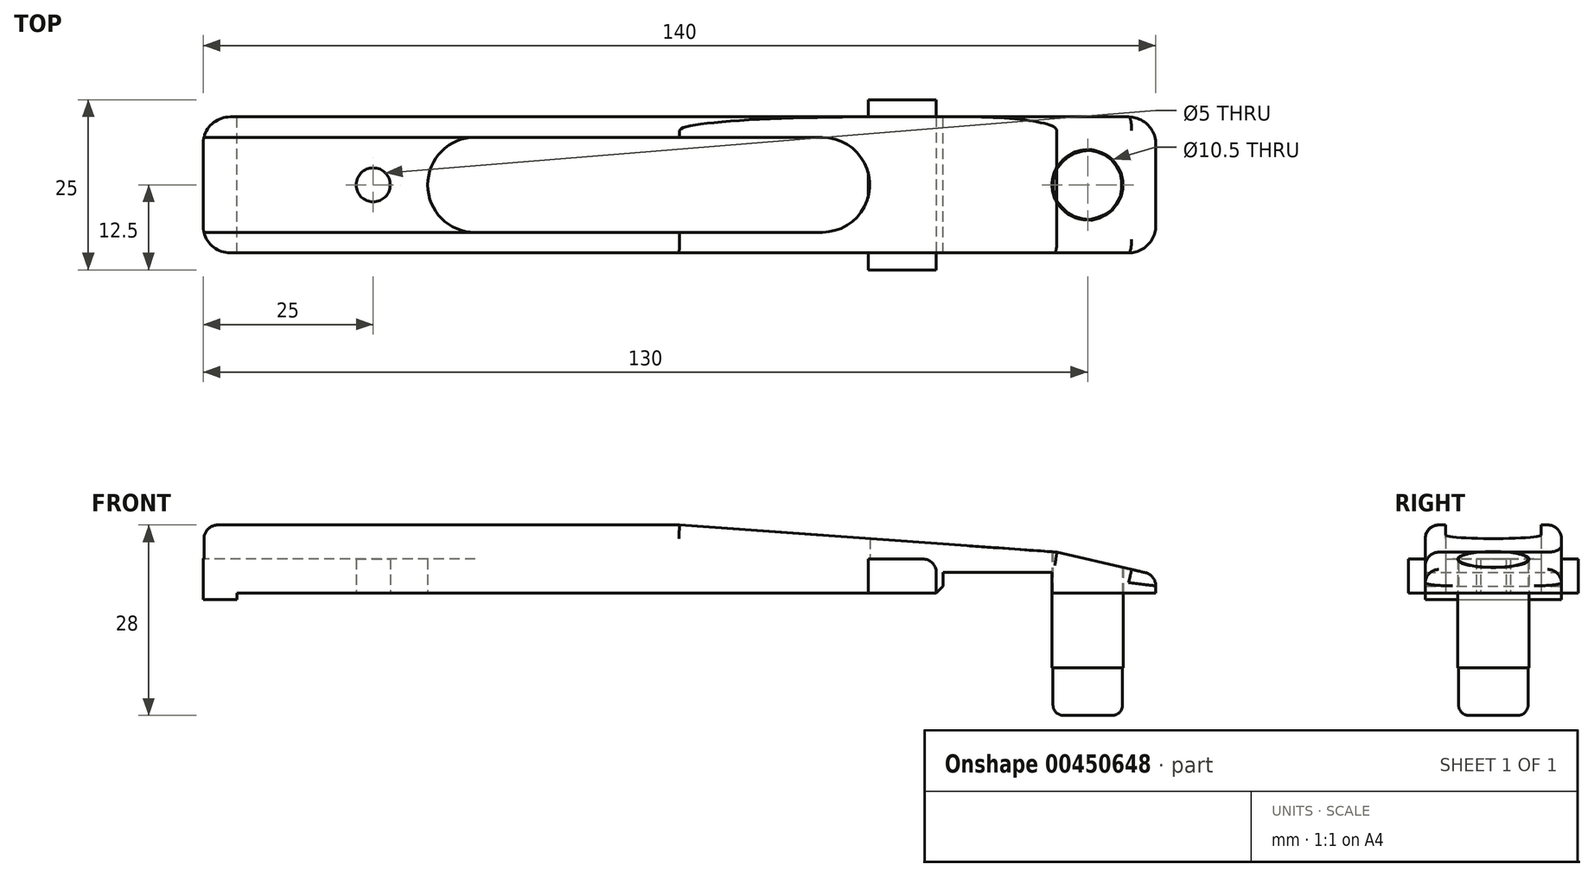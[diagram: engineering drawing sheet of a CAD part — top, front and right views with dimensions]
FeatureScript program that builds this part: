
annotation { "Feature Type Name" : "Feature", "Feature Type Description" : "" }
export const myFeature = defineFeature(function(context is Context, id is Id, definition is map)
    precondition{}
    {
        {
            var Q0;
            Q0=qCreatedBy(makeId("Top.planeOp"),FACE);
            var sketch = newSketch(context, id + "F0", { "sketchPlane" : qUnion([Q0])});
            skLineSegment(sketch, "E0.bottom", {"start": v(66, -10) * mm, "end": v(-66, -10) * mm});
            skLineSegment(sketch, "E0.top", {"start": v(66, 10) * mm, "end": v(-66, 10) * mm});
            skLineSegment(sketch, "E0.left", {"start": v(70, -6) * mm, "end": v(70, 6) * mm});
            skLineSegment(sketch, "E0.right", {"start": v(-70, -6) * mm, "end": v(-70, 6) * mm});
            skPoint(sketch, "E0.middle", {"position": v(0, 0) * mm});
            skCircle(sketch, "E1", {"center": v(-45, 0) * mm, "radius": 2.5 * mm});
            skArc(sketch, "E2", {"start": v(-30, 7) * mm, "mid": v(-37, 0) * mm, "end": v(-30, -7) * mm});
            skArc(sketch, "E3", {"start": v(21, -7) * mm, "mid": v(28, 0) * mm, "end": v(21, 7) * mm});
            skLineSegment(sketch, "E4", {"start": v(-30, 7) * mm, "end": v(21, 7) * mm});
            skLineSegment(sketch, "E5", {"start": v(21, -7) * mm, "end": v(-30, -7) * mm});
            skCircle(sketch, "E6", {"center": v(60, 0) * mm, "radius": 5.1 * mm});
            skPoint(sketch, "E7.visualSharp", {"position": v(-70, 10) * mm});
            skArc(sketch, "E7.filletArc", {"start": v(-66, 10) * mm, "mid": v(-68.83, 8.83) * mm, "end": v(-70, 6) * mm});
            skPoint(sketch, "E8.visualSharp", {"position": v(-70, -10) * mm});
            skArc(sketch, "E8.filletArc", {"start": v(-70, -6) * mm, "mid": v(-68.83, -8.83) * mm, "end": v(-66, -10) * mm});
            skPoint(sketch, "E9.visualSharp", {"position": v(70, 10) * mm});
            skArc(sketch, "E9.filletArc", {"start": v(70, 6) * mm, "mid": v(68.83, 8.83) * mm, "end": v(66, 10) * mm});
            skPoint(sketch, "E10.visualSharp", {"position": v(70, -10) * mm});
            skArc(sketch, "E10.filletArc", {"start": v(66, -10) * mm, "mid": v(68.83, -8.83) * mm, "end": v(70, -6) * mm});
            skCircle(sketch, "E11", {"center": v(60, 0) * mm, "radius": 5.25 * mm});
            skSolve(sketch);
        }
        {
            var Q0;
            Q0=makeQuery(id+"F0.imprint","IMPRINT",FACE,{"disambiguationData":[TD([[makeQuery(id+"F0.imprint","IMPRINT",EDGE,{"derivedFrom":sQuery(id+"F0.wireOp",EDGE,"E0.bottom")}),-1.0]])]});
            extrude(context, id + "F1", {"entities" : qUnion([Q0]), "depth" : 10 * mm, "offsetDistance" : 25 * mm});
        }
        {
            var Q0;
            Q0=makeQuery(id+"F0.imprint","IMPRINT",FACE,{"disambiguationData":[TD([[makeQuery(id+"F0.imprint","IMPRINT",EDGE,{"derivedFrom":sQuery(id+"F0.wireOp",EDGE,"E6")}),1.0]])]});
            extrude(context, id + "F2", {"entities" : qUnion([Q0]), "operationType" : NewBodyOperationType.ADD, "depth" : 10 * mm, "hasSecondDirection" : true, "secondDirectionOppositeDirection" : true, "secondDirectionDepth" : 18 * mm, "offsetDistance" : 25 * mm});
        }
        {
            var Q0;
            Q0=makeQuery(id+"F1.opExtrude","SWEPT_FACE",FACE,{"disambiguationData":[OSD([sQuery(id+"F0.wireOp",EDGE,"E0.right")])]});
            var sketch = newSketch(context, id + "F3", { "sketchPlane" : qUnion([Q0])});
            skLineSegment(sketch, "E12.bottom", {"start": v(-6, 10) * mm, "end": v(7, 10) * mm});
            skLineSegment(sketch, "E12.top", {"start": v(-7, 5) * mm, "end": v(6, 5) * mm});
            skLineSegment(sketch, "E12.left", {"start": v(-7, 10) * mm, "end": v(-7, 5) * mm});
            skLineSegment(sketch, "E12.right", {"start": v(7, 10) * mm, "end": v(7, 5) * mm});
            skLineSegment(sketch, "E13", {"start": v(-7, 10) * mm, "end": v(-6, 10) * mm});
            skLineSegment(sketch, "E14", {"start": v(7, 10) * mm, "end": v(6, 10) * mm});
            skLineSegment(sketch, "E15", {"start": v(7, 5) * mm, "end": v(6, 5) * mm});
            skSolve(sketch);
        }
        {
            var Q0;
            Q0=makeQuery(id+"F3.imprint","IMPRINT",FACE,{"disambiguationData":[TD([[makeQuery(id+"F3.imprint","IMPRINT",EDGE,{"derivedFrom":sQuery(id+"F3.wireOp",EDGE,"E12.bottom")}),1.0]])]});
            var Q1;
            Q1=makeQuery(id+"F3.imprint","IMPRINT",FACE,{"disambiguationData":[TD([[makeQuery(id+"F3.imprint","IMPRINT",EDGE,{"derivedFrom":sQuery(id+"F3.wireOp",EDGE,"E12.right")}),-1.0]])]});
            var Q2;
            {var subQ0=sQuery(id+"F3.wireOp",EDGE,"E12.left");Q2=makeQuery(id+"F3.imprint","IMPRINT",FACE,{"disambiguationData":[TD([[makeQuery(id+"F3.imprint","IMPRINT",EDGE,{"derivedFrom":subQ0}),1.0]])]});}
            extrude(context, id + "F4", {"entities" : qUnion([Q0, Q1, Q2]), "operationType" : NewBodyOperationType.REMOVE, "oppositeDirection" : true, "depth" : 90 * mm});
        }
        {
            var Q0;
            Q0=makeQuery(id+"F1.opExtrude","SWEPT_FACE",FACE,{"disambiguationData":[OSD([sQuery(id+"F0.wireOp",EDGE,"E0.top")])]});
            var sketch = newSketch(context, id + "F5", { "sketchPlane" : qUnion([Q0])});
            skLineSegment(sketch, "E16", {"start": v(-54.74, 0) * mm, "end": v(-54.74, 3) * mm});
            skLineSegment(sketch, "E17", {"start": v(-54.74, 3) * mm, "end": v(-38.74, 3) * mm});
            skLineSegment(sketch, "E18", {"start": v(-38.74, 3) * mm, "end": v(-38.74, 0) * mm});
            skLineSegment(sketch, "E19", {"start": v(-38.74, 0) * mm, "end": v(-54.74, 0) * mm});
            skSolve(sketch);
        }
        {
            var Q0;
            Q0=makeQuery(id+"F5.imprint","IMPRINT",FACE,{"disambiguationData":[TD([[makeQuery(id+"F5.imprint","IMPRINT",EDGE,{"derivedFrom":sQuery(id+"F5.wireOp",EDGE,"E16")}),-1.0]])]});
            extrude(context, id + "F6", {"entities" : qUnion([Q0]), "operationType" : NewBodyOperationType.REMOVE, "oppositeDirection" : true, "depth" : 25 * mm, "offsetDistance" : 25 * mm});
        }
        {
            var Q0;
            Q0=makeQuery(id+"F1.opExtrude","SWEPT_FACE",FACE,{"disambiguationData":[OSD([sQuery(id+"F0.wireOp",EDGE,"E0.top")])]});
            var sketch = newSketch(context, id + "F7", { "sketchPlane" : qUnion([Q0])});
            skLineSegment(sketch, "E20", {"start": v(-81.34, 0) * mm, "end": v(-55.47, 6) * mm});
            skPoint(sketch, "E20.startSnap0", {"position": v(-66, 6) * mm});
            skLineSegment(sketch, "E21", {"start": v(-55.47, 6) * mm, "end": v(0, 10) * mm});
            skLineSegment(sketch, "E22", {"start": v(0, 10) * mm, "end": v(-0.81, 21.29) * mm});
            skLineSegment(sketch, "E23", {"start": v(-0.81, 21.29) * mm, "end": v(-86.16, 20.04) * mm});
            skLineSegment(sketch, "E24", {"start": v(-86.16, 20.04) * mm, "end": v(-81.34, 0) * mm});
            skSolve(sketch);
        }
        {
            var Q0;
            {var subQ4=sQuery(id+"F7.wireOp",EDGE,"E22");Q0=makeQuery(id+"F7.imprint","IMPRINT",FACE,{"disambiguationData":[TD([[makeQuery(id+"F7.imprint","IMPRINT",EDGE,{"derivedFrom":subQ4}),1.0]])]});}
            var Q1;
            {var subQ0=sQuery(id+"F7.wireOp",EDGE,"E21");Q1=makeQuery(id+"F7.imprint","IMPRINT",FACE,{"disambiguationData":[TD([[makeQuery(id+"F7.imprint","IMPRINT",EDGE,{"derivedFrom":subQ0}),1.0]])]});}
            extrude(context, id + "F8", {"entities" : qUnion([Q0, Q1]), "operationType" : NewBodyOperationType.REMOVE, "oppositeDirection" : true, "depth" : 25 * mm, "offsetDistance" : 25 * mm});
        }
        {
            var Q0;
            Q0=makeQuery(id+"F2.opExtrude","CAP_EDGE",EDGE,{"disambiguationData":[OSD([sQuery(id+"F0.wireOp",EDGE,"E6")])],"isStart":true});
            fillet(context, id + "F9", {"entities" : qUnion([Q0]), "radius" : 1.5 * mm, "tangentPropagation" : true, "allowEdgeOverflow" : false});
        }
        {
            var Q0;
            Q0=makeQuery(id+"F8.boolean.opBoolean","INTERSECT",EDGE,{"derivedFrom":[makeQuery(id+"F1.opExtrude","SWEPT_FACE",FACE,{"disambiguationData":[OSD([sQuery(id+"F0.wireOp",EDGE,"E0.bottom")])]}),makeQuery(id+"F8.opExtrude","SWEPT_FACE",FACE,{"disambiguationData":[OSD([sQuery(id+"F7.wireOp",EDGE,"E21")])]})]});
            var Q1;
            Q1=makeQuery(id+"F8.boolean.opBoolean","INTERSECT",EDGE,{"derivedFrom":[makeQuery(id+"F1.opExtrude","SWEPT_FACE",FACE,{"disambiguationData":[OSD([sQuery(id+"F0.wireOp",EDGE,"E10.filletArc")])]}),makeQuery(id+"F8.opExtrude","SWEPT_FACE",FACE,{"disambiguationData":[OSD([sQuery(id+"F7.wireOp",EDGE,"E20")])]})]});
            var Q2;
            Q2=makeQuery(id+"F8.boolean.opBoolean","COPY",EDGE,{"derivedFrom":makeQuery(id+"F8.opExtrude","CAP_EDGE",EDGE,{"disambiguationData":[OSD([sQuery(id+"F7.wireOp",EDGE,"E21")])],"isStart":true})});
            var Q3;
            Q3=makeQuery(id+"F1.opExtrude","CAP_EDGE",EDGE,{"disambiguationData":[OSD([sQuery(id+"F0.wireOp",EDGE,"E0.bottom")])],"isStart":false});
            var Q4;
            Q4=makeQuery(id+"F1.opExtrude","CAP_EDGE",EDGE,{"disambiguationData":[OSD([sQuery(id+"F0.wireOp",EDGE,"E0.top")])],"isStart":false});
            fillet(context, id + "F10", {"entities" : qUnion([Q0, Q1, Q2, Q3, Q4]), "radius" : 2 * mm, "tangentPropagation" : true, "allowEdgeOverflow" : false});
        }
        {
            var Q0;
            Q0=makeQuery(id+"F0.imprint","IMPRINT",FACE,{"disambiguationData":[TD([[makeQuery(id+"F0.imprint","IMPRINT",EDGE,{"derivedFrom":sQuery(id+"F0.wireOp",EDGE,"E6")}),-1.0]])]});
            var Q1;
            Q1=makeQuery(id+"F0.imprint","IMPRINT",FACE,{"disambiguationData":[TD([[makeQuery(id+"F0.imprint","IMPRINT",EDGE,{"derivedFrom":sQuery(id+"F0.wireOp",EDGE,"E6")}),1.0]])]});
            extrude(context, id + "F11", {"entities" : qUnion([Q0, Q1]), "operationType" : NewBodyOperationType.ADD, "oppositeDirection" : true, "depth" : 11 * mm, "offsetDistance" : 25 * mm});
        }
        {
            var Q0;
            Q0=makeQuery(id+"F1.opExtrude","SWEPT_FACE",FACE,{"disambiguationData":[OSD([sQuery(id+"F0.wireOp",EDGE,"E0.bottom")])]});
            var sketch = newSketch(context, id + "F12", { "sketchPlane" : qUnion([Q0])});
            skSolve(sketch);
        }
        {
            var Q0;
            {var subQ4=sQuery(id+"F7.wireOp",EDGE,"E22");Q0=makeQuery(id+"F7.imprint","IMPRINT",FACE,{"disambiguationData":[TD([[makeQuery(id+"F7.imprint","IMPRINT",EDGE,{"derivedFrom":subQ4}),1.0]])]});}
            var Q1;
            {var subQ0=sQuery(id+"F7.wireOp",EDGE,"E21");Q1=makeQuery(id+"F7.imprint","IMPRINT",FACE,{"disambiguationData":[TD([[makeQuery(id+"F7.imprint","IMPRINT",EDGE,{"derivedFrom":subQ0}),1.0]])]});}
            extrude(context, id + "F13", {"entities" : qUnion([Q0, Q1]), "operationType" : NewBodyOperationType.REMOVE, "oppositeDirection" : true, "depth" : 25 * mm, "offsetDistance" : 25 * mm});
        }
        {
            var Q0;
            Q0=makeQuery(id+"F0.imprint","IMPRINT",FACE,{"disambiguationData":[TD([[makeQuery(id+"F0.imprint","IMPRINT",EDGE,{"derivedFrom":sQuery(id+"F0.wireOp",EDGE,"E6")}),-1.0]])]});
            extrude(context, id + "F14", {"entities" : qUnion([Q0]), "depth" : 25 * mm, "offsetDistance" : 25 * mm});
        }
        {
            var Q0;
            {var subQ4=sQuery(id+"F7.wireOp",EDGE,"E22");Q0=makeQuery(id+"F7.imprint","IMPRINT",FACE,{"disambiguationData":[TD([[makeQuery(id+"F7.imprint","IMPRINT",EDGE,{"derivedFrom":subQ4}),1.0]])]});}
            var Q1;
            {var subQ0=sQuery(id+"F7.wireOp",EDGE,"E21");Q1=makeQuery(id+"F7.imprint","IMPRINT",FACE,{"disambiguationData":[TD([[makeQuery(id+"F7.imprint","IMPRINT",EDGE,{"derivedFrom":subQ0}),1.0]])]});}
            extrude(context, id + "F15", {"entities" : qUnion([Q0, Q1]), "operationType" : NewBodyOperationType.REMOVE, "oppositeDirection" : true, "depth" : 25 * mm, "offsetDistance" : 25 * mm});
        }
        {
            var Q0;
            Q0=makeQuery(id+"F15.boolean.opBoolean","SPLIT",BODY,{"disambiguationData":[OD(1.0)],"derivedFrom":makeQuery(id+"F14.opExtrude","SWEPT_BODY",BODY,{"disambiguationData":[OSD([sQuery(id+"F0.wireOp",EDGE,"E6"),sQuery(id+"F0.wireOp",EDGE,"E11")])]})});
            deleteBodies(context, id + "F16", {"entities" : qUnion([Q0])});
        }
        {
            var Q0;
            Q0=makeQuery(id+"F6.boolean.opBoolean","COPY",EDGE,{"derivedFrom":makeQuery(id+"F6.opExtrude","SWEPT_EDGE",EDGE,{"disambiguationData":[OSD([sQuery(id+"F0.wireOp",EDGE,"E0.top"),sQuery(id+"F5.wireOp",EDGE,"E18"),sQuery(id+"F5.wireOp",EDGE,"E19")])]})});
            chamfer(context, id + "F17", {"entities" : qUnion([Q0]), "width" : 1 * mm, "tangentPropagation" : true});
        }
        {
            var Q0;
            Q0=makeQuery(id+"F1.opExtrude","SWEPT_FACE",FACE,{"disambiguationData":[OSD([sQuery(id+"F0.wireOp",EDGE,"E0.top")])]});
            var sketch = newSketch(context, id + "F18", { "sketchPlane" : qUnion([Q0])});
            skLineSegment(sketch, "E25.bottom", {"start": v(-37.74, 0) * mm, "end": v(-27.74, 0) * mm});
            skLineSegment(sketch, "E25.top", {"start": v(-35.74, 5) * mm, "end": v(-27.74, 5) * mm});
            skLineSegment(sketch, "E25.left", {"start": v(-37.74, 0) * mm, "end": v(-37.74, 3) * mm});
            skLineSegment(sketch, "E25.right", {"start": v(-27.74, 0) * mm, "end": v(-27.74, 5) * mm});
            skPoint(sketch, "E26.visualSharp", {"position": v(-37.74, 5) * mm});
            skArc(sketch, "E26.filletArc", {"start": v(-35.74, 5) * mm, "mid": v(-37.15, 4.41) * mm, "end": v(-37.74, 3) * mm});
            skSolve(sketch);
        }
        {
            var Q0;
            Q0=makeQuery(id+"F18.imprint","IMPRINT",FACE,{"disambiguationData":[TD([[makeQuery(id+"F18.imprint","IMPRINT",EDGE,{"derivedFrom":sQuery(id+"F18.wireOp",EDGE,"E25.bottom")}),1.0]])]});
            extrude(context, id + "F19", {"entities" : qUnion([Q0]), "operationType" : NewBodyOperationType.ADD, "depth" : 2.5 * mm, "offsetDistance" : 25 * mm, "hasSecondDirection" : true, "secondDirectionOppositeDirection" : true, "secondDirectionDepth" : 22.5 * mm});
        }
        {
            var Q0;
            {var subQ0=sQuery(id+"F0.wireOp",EDGE,"E8.filletArc");var subQ1=sQuery(id+"F0.wireOp",EDGE,"E5");var subQ2=sQuery(id+"F0.wireOp",EDGE,"E4");var subQ3=sQuery(id+"F0.wireOp",EDGE,"E3");var subQ4=sQuery(id+"F0.wireOp",EDGE,"E2");var subQ5=sQuery(id+"F0.wireOp",EDGE,"E7.filletArc");var subQ6=sQuery(id+"F0.wireOp",EDGE,"E0.bottom");var subQ7=sQuery(id+"F0.wireOp",EDGE,"E0.right");var subQ8=sQuery(id+"F0.wireOp",EDGE,"E0.top");var subQ9=sQuery(id+"F0.wireOp",EDGE,"E1");Q0=makeQuery(id+"F19.boolean.opBoolean","MERGE",FACE,{"derivedFrom":[makeQuery(id+"F6.boolean.opBoolean","SPLIT",FACE,{"disambiguationData":[TD([makeQuery(id+"F1.opExtrude","SWEPT_FACE",FACE,{"disambiguationData":[OSD([subQ7])]})])],"derivedFrom":makeQuery(id+"F1.opExtrude","CAP_FACE",FACE,{"disambiguationData":[OSD([subQ6,subQ8,sQuery(id+"F0.wireOp",EDGE,"E0.left"),subQ7,subQ9,subQ4,subQ3,subQ2,subQ1,subQ5,subQ0,sQuery(id+"F0.wireOp",EDGE,"E9.filletArc"),sQuery(id+"F0.wireOp",EDGE,"E10.filletArc"),sQuery(id+"F0.wireOp",EDGE,"E11")])],"isStart":true})}),makeQuery(id+"F19.opExtrude","SWEPT_FACE",FACE,{"disambiguationData":[OSD([sQuery(id+"F18.wireOp",EDGE,"E25.bottom")])]})]});}
            var sketch = newSketch(context, id + "F20", { "sketchPlane" : qUnion([Q0])});
            skLineSegment(sketch, "E27", {"start": v(-65, 10) * mm, "end": v(-65, -10) * mm});
            skSolve(sketch);
        }
        {
            var Q0;
            {var subQ9=sQuery(id+"F20.wireOp",EDGE,"E27");Q0=makeQuery(id+"F20.imprint","IMPRINT",FACE,{"disambiguationData":[TD([[makeQuery(id+"F20.imprint","IMPRINT",EDGE,{"derivedFrom":subQ9}),-1.0]])]});}
            extrude(context, id + "F21", {"entities" : qUnion([Q0]), "operationType" : NewBodyOperationType.ADD, "depth" : 1 * mm, "offsetDistance" : 25 * mm});
        }
    });
